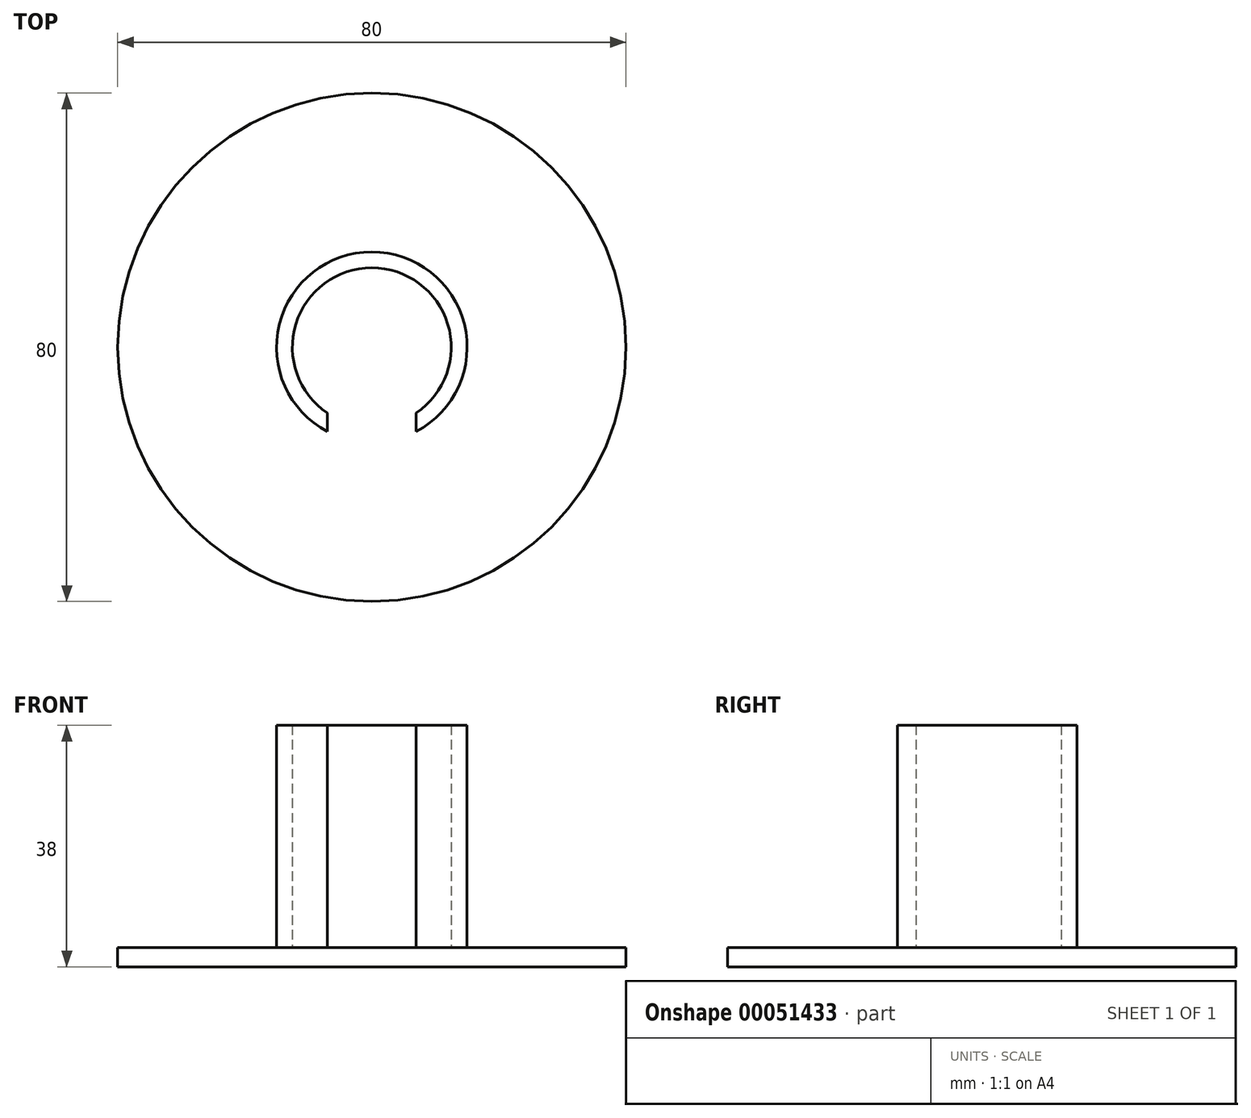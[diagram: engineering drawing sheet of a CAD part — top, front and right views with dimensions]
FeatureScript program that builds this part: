
annotation { "Feature Type Name" : "Feature", "Feature Type Description" : "" }
export const myFeature = defineFeature(function(context is Context, id is Id, definition is map)
    precondition{}
    {
        {
            var Q0;
            Q0=qCreatedBy(makeId("Top.planeOp"),FACE);
            var sketch = newSketch(context, id + "F0", { "sketchPlane" : qUnion([Q0])});
            skCircle(sketch, "E0", {"center": v(0, 0) * mm, "radius": 40 * mm});
            skSolve(sketch);
        }
        {
            var Q0;
            Q0=qSketchRegion(id+"F0",true);
            extrude(context, id + "F1", {"entities" : qUnion([Q0]), "depth" : 3 * mm});
        }
        {
            var Q0;
            Q0=makeQuery(id+"F1.opExtrude","CAP_FACE",FACE,{"disambiguationData":[OSD([sQuery(id+"F0.wireOp",EDGE,"E0")])],"isStart":false});
            var sketch = newSketch(context, id + "F2", { "sketchPlane" : qUnion([Q0])});
            skCircle(sketch, "E1", {"center": v(0, 0) * mm, "radius": 12.5 * mm});
            skCircle(sketch, "E2", {"center": v(0, 0) * mm, "radius": 15 * mm});
            skSolve(sketch);
        }
        {
            var Q0;
            Q0=qSketchRegion(id+"F2",true);
            var Q1;
            Q1=sQuery(id+"F2.wireOp",EDGE,"E2");
            var Q2;
            Q2=sQuery(id+"F2.wireOp",EDGE,"E1");
            extrude(context, id + "F3", {"entities" : qUnion([Q0]), "operationType" : NewBodyOperationType.ADD, "surfaceEntities" : qUnion([Q1, Q2]), "depth" : 35 * mm});
        }
        {
            var Q0;
            Q0=makeQuery(id+"F3.opExtrude","CAP_FACE",FACE,{"disambiguationData":[OSD([sQuery(id+"F2.wireOp",EDGE,"E1"),sQuery(id+"F2.wireOp",EDGE,"E2")])],"isStart":false});
            var sketch = newSketch(context, id + "F4", { "sketchPlane" : qUnion([Q0])});
            skLineSegment(sketch, "E3.bottom", {"start": v(-7, 0) * mm, "end": v(7, 0) * mm});
            skLineSegment(sketch, "E3.top", {"start": v(-7, -50) * mm, "end": v(7, -50) * mm});
            skLineSegment(sketch, "E3.left", {"start": v(-7, 0) * mm, "end": v(-7, -50) * mm});
            skLineSegment(sketch, "E3.right", {"start": v(7, 0) * mm, "end": v(7, -50) * mm});
            skSolve(sketch);
        }
        {
            var Q0;
            Q0=qSketchRegion(id+"F4",true);
            extrude(context, id + "F5", {"entities" : qUnion([Q0]), "operationType" : NewBodyOperationType.REMOVE, "oppositeDirection" : true, "depth" : 35 * mm});
        }
    });
